# Revit family: SAM-3001_GENERADO
name_source: partatom
category: Equipos mecánicos
revit_build: Autodesk Revit 2014 (Build: 20130308_1515(x64)
units: mm (PartAtom-declared; Revit-internal decimal feet)

## types (4) — shared parameters
Comentarios de tipo = Tabletop cutlery polishing machine with outlet fan.
Depth = 652 mm  [stored 2.13911 ft]
Fabricante = SAMMIC S.L.
Foodservice Equipment Identifier = Sí
HP = 0.78
Height = 412 mm  [stored 1.35171 ft]
Revision Code = 1
Specification by Manufacturer = Output: 3000 pieces per hour.
URL = https://www.sammic.com
Watts = 580 W
Width = 489 mm  [stored 1.60433 ft]

## per-type parameters (varying)
| type | Cycle | Electric Connection Type | FL Amps | Modelo | URL Cutsheet | Volts | Weight in Pounds |
| Cutlery dryer SAM-3001  230/50/1 | 50 Hz | EU | 3 A | 1370043 | http://www.sammic.com | 230 V | 93.3 |
| Cutlery dryer SAM-3001 220/60/1 | 60 Hz | EU | 3 A | 1370045 | http://www.sammic.com | 220 V | 93.3 |
| Cutlery dryer SAM-3001 120/60/1 | 60 Hz | USA | 5 A | 1370058 | http://www.sammic.com | 120 V | 93.3 |
| Cutlery dryer SAM-3001 220/60/1 KSA | 60 Hz |  | 3 A | 1370065 |  | 220 V | 94.8 |

note: column(s) folded — value = type name in every type: Descripción

note: [stored X ft] marks values corroborated as IEEE doubles in the binary element streams (Revit-internal decimal feet)
